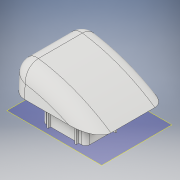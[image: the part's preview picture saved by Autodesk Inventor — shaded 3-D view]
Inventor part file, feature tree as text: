
AUTODESK INVENTOR PART (.ipt)
format: ipt  version: 2017 (Build 210142000, 142)  size: 386,048 bytes
history: native  units: in
note: dims shown in document units (in); Inventor stores cm internally (conversion verified against a paired STEP export)
features: sketch x3, extrude x2, fillet x2, shell x1, plane x1, projected_geometry x1
ambient origin geometry x8: Origin, YZ Plane, XZ Plane, XY Plane, X Axis, Y Axis, Z Axis, Center Point
bodies: Solid1 (feature_tree)
feature tree (10):
  extrude  "Extrusion1"  Depth=6.0in
  fillet  "Fillet1"  Radius=0.64in
  fillet  "Fillet2"  Radius=3.01in
  shell  "Shell1"  Thickness=6.0in
  plane  "Work Plane2"
  sketch  "Sketch3"  dims[d12=0.4in d13=2.55in d14=0.0in]
  extrude  "Extrusion2"  Depth=2.55in TaperAngle=0.0deg
  sketch  "Sketch1"  dims[d0=3.04in d6=6.0in d8=0.64in d10=3.01in d11=6.0in]
  sketch  "Sketch4"  dims[d15=0.5in d16=0.5in d17=0.1in d19=0.67in d20=0.68in d21=2.22in d22=2.26in d23=0.29in d24=0.15in d25=0.05in d26=0.95in d27=1.94in d28=1.28in d29=0.09in d30=0.025in d31=0.05in d32=0.09in d33=0.05in d34=0.025in d35=0.09in d36=0.05in d37=0.025in d38=0.09in d39=0.09in d40=0.05in d41=0.025in d42=0.09in d43=0.05in d44=0.025in d45=2.55in d46=0.0in]
  projected_geometry  "Projected Loop1"
